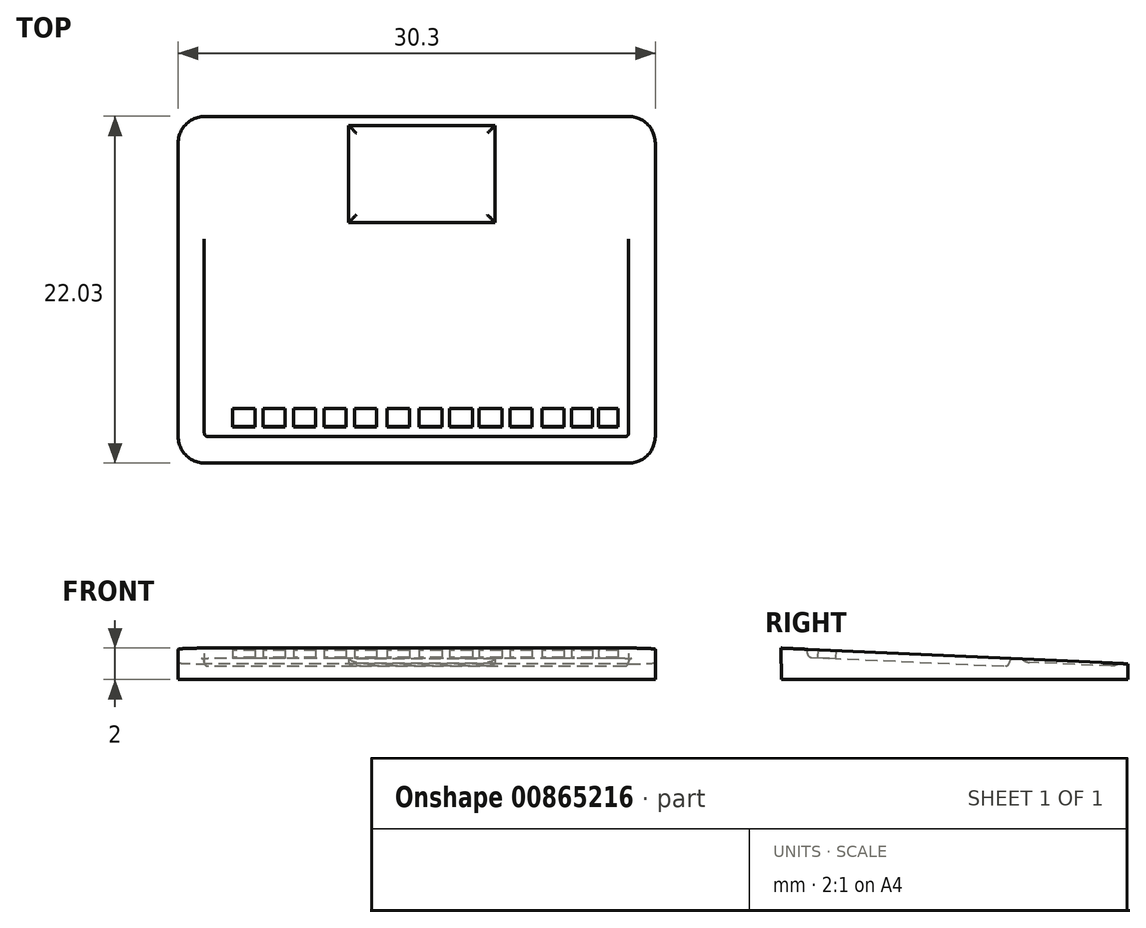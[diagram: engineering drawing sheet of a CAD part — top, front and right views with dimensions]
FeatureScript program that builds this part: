
annotation { "Feature Type Name" : "Feature", "Feature Type Description" : "" }
export const myFeature = defineFeature(function(context is Context, id is Id, definition is map)
    precondition{}
    {
        {
            var Q0;
            Q0=qCreatedBy(makeId("Right.planeOp"),FACE);
            var sketch = newSketch(context, id + "F0", { "sketchPlane" : qUnion([Q0])});
            skLineSegment(sketch, "E0", {"start": v(-240.72, 0) * mm, "end": v(-218.72, 0) * mm});
            skLineSegment(sketch, "E1", {"start": v(-218.72, 0) * mm, "end": v(-218.72, 1) * mm});
            skLineSegment(sketch, "E2", {"start": v(-218.72, 1) * mm, "end": v(-242.1, 41.92) * mm});
            skLineSegment(sketch, "E3", {"start": v(-242.1, 41.92) * mm, "end": v(-240.72, 0) * mm});
            skLineSegment(sketch, "E4", {"start": v(-44.13, 0) * mm, "end": v(-22.13, 0) * mm});
            skLineSegment(sketch, "E5", {"start": v(-22.13, 0) * mm, "end": v(-22.13, 1) * mm});
            skLineSegment(sketch, "E6", {"start": v(-22.13, 1) * mm, "end": v(-44.16, 2) * mm});
            skLineSegment(sketch, "E7", {"start": v(-44.16, 2) * mm, "end": v(-44.13, 0) * mm});
            skSolve(sketch);
        }
        {
            var Q0;
            Q0=makeQuery(id+"F0.imprint","IMPRINT",FACE,{"disambiguationData":[TD([[makeQuery(id+"F0.imprint","IMPRINT",EDGE,{"derivedFrom":sQuery(id+"F0.wireOp",EDGE,"E4")}),1.0]])]});
            extrude(context, id + "F1", {"entities" : qUnion([Q0]), "depth" : 30.3 * mm, "offsetDistance" : 25 * mm});
        }
        {
            var Q0;
            Q0=makeQuery(id+"F1.opExtrude","CAP_EDGE",EDGE,{"disambiguationData":[OSD([sQuery(id+"F0.wireOp",EDGE,"E5")])],"isStart":true});
            var Q1;
            Q1=makeQuery(id+"F1.opExtrude","CAP_EDGE",EDGE,{"disambiguationData":[OSD([sQuery(id+"F0.wireOp",EDGE,"E5")])],"isStart":false});
            var Q2;
            Q2=makeQuery(id+"F1.opExtrude","CAP_EDGE",EDGE,{"disambiguationData":[OSD([sQuery(id+"F0.wireOp",EDGE,"E7")])],"isStart":false});
            var Q3;
            Q3=makeQuery(id+"F1.opExtrude","CAP_EDGE",EDGE,{"disambiguationData":[OSD([sQuery(id+"F0.wireOp",EDGE,"E7")])],"isStart":true});
            fillet(context, id + "F2", {"entities" : qUnion([Q0, Q1, Q2, Q3]), "radius" : 1.69 * mm, "tangentPropagation" : true, "allowEdgeOverflow" : false});
        }
        {
            var Q0;
            Q0=makeQuery(id+"F1.opExtrude","SWEPT_FACE",FACE,{"disambiguationData":[OSD([sQuery(id+"F0.wireOp",EDGE,"E6")])]});
            var sketch = newSketch(context, id + "F3", { "sketchPlane" : qUnion([Q0])});
            skLineSegment(sketch, "E8.bottom", {"start": v(28.61, -42.52) * mm, "end": v(1.66, -42.52) * mm});
            skLineSegment(sketch, "E8.top", {"start": v(28.61, -29.7) * mm, "end": v(1.66, -29.7) * mm});
            skLineSegment(sketch, "E8.left", {"start": v(28.61, -42.52) * mm, "end": v(28.61, -29.7) * mm});
            skLineSegment(sketch, "E8.right", {"start": v(1.66, -42.52) * mm, "end": v(1.66, -29.7) * mm});
            skSolve(sketch);
        }
        {
            var Q0;
            Q0 = qSketchRegion(id + "F3", true);
            extrude(context, id + "F4", {"entities" : qUnion([Q0]), "operationType" : NewBodyOperationType.REMOVE, "oppositeDirection" : true, "depth" : 0.5 * mm, "offsetDistance" : 25 * mm});
        }
        {
            var Q0;
            Q0=makeQuery(id+"F4.boolean.opBoolean","COPY",FACE,{"derivedFrom":makeQuery(id+"F4.opExtrude","SWEPT_FACE",FACE,{"disambiguationData":[OSD([sQuery(id+"F3.wireOp",EDGE,"E8.bottom")])]})});
            var Q1;
            Q1=makeQuery(id+"F4.boolean.opBoolean","COPY",EDGE,{"derivedFrom":makeQuery(id+"F4.opExtrude","CAP_EDGE",EDGE,{"disambiguationData":[OSD([sQuery(id+"F3.wireOp",EDGE,"E8.right")])],"isStart":true})});
            var Q2;
            Q2=makeQuery(id+"F4.boolean.opBoolean","COPY",FACE,{"derivedFrom":makeQuery(id+"F4.opExtrude","SWEPT_FACE",FACE,{"disambiguationData":[OSD([sQuery(id+"F3.wireOp",EDGE,"E8.right")])]})});
            var Q3;
            Q3=makeQuery(id+"F4.boolean.opBoolean","COPY",FACE,{"derivedFrom":makeQuery(id+"F4.opExtrude","SWEPT_FACE",FACE,{"disambiguationData":[OSD([sQuery(id+"F3.wireOp",EDGE,"E8.top")])]})});
            var Q4;
            Q4=makeQuery(id+"F4.boolean.opBoolean","COPY",FACE,{"derivedFrom":makeQuery(id+"F4.opExtrude","SWEPT_FACE",FACE,{"disambiguationData":[OSD([sQuery(id+"F3.wireOp",EDGE,"E8.left")])]})});
            fillet(context, id + "F5", {"entities" : qUnion([Q0, Q1, Q2, Q3, Q4]), "radius" : 0.24 * mm, "tangentPropagation" : true, "allowEdgeOverflow" : false});
        }
        {
            var Q0;
            Q0=makeQuery(id+"F4.boolean.opBoolean","COPY",FACE,{"derivedFrom":makeQuery(id+"F4.opExtrude","CAP_FACE",FACE,{"disambiguationData":[OSD([sQuery(id+"F3.wireOp",EDGE,"E8.bottom"),sQuery(id+"F3.wireOp",EDGE,"E8.top"),sQuery(id+"F3.wireOp",EDGE,"E8.left"),sQuery(id+"F3.wireOp",EDGE,"E8.right")])],"isStart":false})});
            var sketch = newSketch(context, id + "F6", { "sketchPlane" : qUnion([Q0])});
            skLineSegment(sketch, "E9.bottom", {"start": v(27.93, -41.88) * mm, "end": v(26.7, -41.88) * mm});
            skLineSegment(sketch, "E9.top", {"start": v(27.93, -40.74) * mm, "end": v(26.7, -40.74) * mm});
            skLineSegment(sketch, "E9.left", {"start": v(27.93, -41.88) * mm, "end": v(27.93, -40.74) * mm});
            skLineSegment(sketch, "E9.right", {"start": v(26.7, -41.88) * mm, "end": v(26.7, -40.74) * mm});
            skPoint(sketch, "E10.firstSnap0", {"position": v(27.32, -41.88) * mm});
            skLineSegment(sketch, "E10.bottom", {"start": v(26.33, -41.88) * mm, "end": v(24.98, -41.88) * mm});
            skLineSegment(sketch, "E10.top", {"start": v(26.33, -40.73) * mm, "end": v(24.98, -40.73) * mm});
            skLineSegment(sketch, "E10.left", {"start": v(26.33, -41.88) * mm, "end": v(26.33, -40.73) * mm});
            skLineSegment(sketch, "E10.right", {"start": v(24.98, -41.88) * mm, "end": v(24.98, -40.73) * mm});
            skLineSegment(sketch, "E11.bottom", {"start": v(24.5, -41.88) * mm, "end": v(23.1, -41.88) * mm});
            skLineSegment(sketch, "E11.top", {"start": v(24.5, -40.73) * mm, "end": v(23.1, -40.73) * mm});
            skLineSegment(sketch, "E11.left", {"start": v(24.5, -41.88) * mm, "end": v(24.5, -40.73) * mm});
            skLineSegment(sketch, "E11.right", {"start": v(23.1, -41.88) * mm, "end": v(23.1, -40.73) * mm});
            skLineSegment(sketch, "E12.bottom", {"start": v(22.49, -41.88) * mm, "end": v(21.08, -41.88) * mm});
            skLineSegment(sketch, "E12.top", {"start": v(22.49, -40.73) * mm, "end": v(21.08, -40.73) * mm});
            skLineSegment(sketch, "E12.left", {"start": v(22.49, -41.88) * mm, "end": v(22.49, -40.73) * mm});
            skLineSegment(sketch, "E12.right", {"start": v(21.08, -41.88) * mm, "end": v(21.08, -40.73) * mm});
            skLineSegment(sketch, "E13.bottom", {"start": v(20.56, -41.88) * mm, "end": v(19.12, -41.88) * mm});
            skLineSegment(sketch, "E13.top", {"start": v(20.56, -40.73) * mm, "end": v(19.12, -40.73) * mm});
            skLineSegment(sketch, "E13.left", {"start": v(20.56, -41.88) * mm, "end": v(20.56, -40.73) * mm});
            skLineSegment(sketch, "E13.right", {"start": v(19.12, -41.88) * mm, "end": v(19.12, -40.73) * mm});
            skLineSegment(sketch, "E14.bottom", {"start": v(18.7, -41.88) * mm, "end": v(17.23, -41.88) * mm});
            skLineSegment(sketch, "E14.top", {"start": v(18.7, -40.73) * mm, "end": v(17.23, -40.73) * mm});
            skLineSegment(sketch, "E14.left", {"start": v(18.7, -41.88) * mm, "end": v(18.7, -40.73) * mm});
            skLineSegment(sketch, "E14.right", {"start": v(17.23, -41.88) * mm, "end": v(17.23, -40.73) * mm});
            skLineSegment(sketch, "E15.bottom", {"start": v(16.75, -41.88) * mm, "end": v(15.3, -41.88) * mm});
            skLineSegment(sketch, "E15.top", {"start": v(16.75, -40.73) * mm, "end": v(15.3, -40.73) * mm});
            skLineSegment(sketch, "E15.left", {"start": v(16.75, -41.88) * mm, "end": v(16.75, -40.73) * mm});
            skLineSegment(sketch, "E15.right", {"start": v(15.3, -41.88) * mm, "end": v(15.3, -40.73) * mm});
            skLineSegment(sketch, "E16.bottom", {"start": v(14.7, -41.88) * mm, "end": v(13.27, -41.88) * mm});
            skLineSegment(sketch, "E16.top", {"start": v(14.7, -40.73) * mm, "end": v(13.27, -40.73) * mm});
            skLineSegment(sketch, "E16.left", {"start": v(14.7, -41.88) * mm, "end": v(14.7, -40.73) * mm});
            skLineSegment(sketch, "E16.right", {"start": v(13.27, -41.88) * mm, "end": v(13.27, -40.73) * mm});
            skLineSegment(sketch, "E17.bottom", {"start": v(12.6, -41.88) * mm, "end": v(11.19, -41.88) * mm});
            skLineSegment(sketch, "E17.top", {"start": v(12.6, -40.73) * mm, "end": v(11.19, -40.73) * mm});
            skLineSegment(sketch, "E17.left", {"start": v(12.6, -41.88) * mm, "end": v(12.6, -40.73) * mm});
            skLineSegment(sketch, "E17.right", {"start": v(11.19, -41.88) * mm, "end": v(11.19, -40.73) * mm});
            skLineSegment(sketch, "E18.bottom", {"start": v(10.67, -41.88) * mm, "end": v(9.26, -41.88) * mm});
            skLineSegment(sketch, "E18.top", {"start": v(10.67, -40.73) * mm, "end": v(9.26, -40.73) * mm});
            skLineSegment(sketch, "E18.left", {"start": v(10.67, -41.88) * mm, "end": v(10.67, -40.73) * mm});
            skLineSegment(sketch, "E18.right", {"start": v(9.26, -41.88) * mm, "end": v(9.26, -40.73) * mm});
            skLineSegment(sketch, "E19.bottom", {"start": v(8.74, -41.88) * mm, "end": v(7.32, -41.88) * mm});
            skLineSegment(sketch, "E19.top", {"start": v(8.74, -40.73) * mm, "end": v(7.32, -40.73) * mm});
            skLineSegment(sketch, "E19.left", {"start": v(8.74, -41.88) * mm, "end": v(8.74, -40.73) * mm});
            skLineSegment(sketch, "E19.right", {"start": v(7.32, -41.88) * mm, "end": v(7.32, -40.73) * mm});
            skLineSegment(sketch, "E20.bottom", {"start": v(6.79, -41.88) * mm, "end": v(5.38, -41.88) * mm});
            skLineSegment(sketch, "E20.top", {"start": v(6.79, -40.73) * mm, "end": v(5.38, -40.73) * mm});
            skLineSegment(sketch, "E20.left", {"start": v(6.79, -41.88) * mm, "end": v(6.79, -40.73) * mm});
            skLineSegment(sketch, "E20.right", {"start": v(5.38, -41.88) * mm, "end": v(5.38, -40.73) * mm});
            skLineSegment(sketch, "E21.bottom", {"start": v(4.9, -41.88) * mm, "end": v(3.46, -41.88) * mm});
            skLineSegment(sketch, "E21.top", {"start": v(4.9, -40.73) * mm, "end": v(3.46, -40.73) * mm});
            skLineSegment(sketch, "E21.left", {"start": v(4.9, -41.88) * mm, "end": v(4.9, -40.73) * mm});
            skLineSegment(sketch, "E21.right", {"start": v(3.46, -41.88) * mm, "end": v(3.46, -40.73) * mm});
            skSolve(sketch);
        }
        {
            var Q0;
            Q0 = qSketchRegion(id + "F6", true);
            extrude(context, id + "F7", {"entities" : qUnion([Q0]), "operationType" : NewBodyOperationType.ADD, "depth" : 0.5 * mm, "offsetDistance" : 25 * mm});
        }
        {
            var Q0;
            Q0=makeQuery(id+"F1.opExtrude","SWEPT_FACE",FACE,{"disambiguationData":[OSD([sQuery(id+"F0.wireOp",EDGE,"E6")])]});
            var sketch = newSketch(context, id + "F8", { "sketchPlane" : qUnion([Q0])});
            skLineSegment(sketch, "E22.bottom", {"start": v(20.13, -28.9) * mm, "end": v(10.83, -28.9) * mm});
            skLineSegment(sketch, "E22.top", {"start": v(20.13, -22.74) * mm, "end": v(10.83, -22.74) * mm});
            skLineSegment(sketch, "E22.left", {"start": v(20.13, -28.9) * mm, "end": v(20.13, -22.74) * mm});
            skLineSegment(sketch, "E22.right", {"start": v(10.83, -28.9) * mm, "end": v(10.83, -22.74) * mm});
            skSolve(sketch);
        }
        {
            var Q0;
            Q0 = qSketchRegion(id + "F8", true);
            extrude(context, id + "F9", {"entities" : qUnion([Q0]), "operationType" : NewBodyOperationType.REMOVE, "oppositeDirection" : true, "depth" : 0.19 * mm, "offsetDistance" : 25 * mm});
        }
        {
            var Q0;
            Q0=makeQuery(id+"F9.boolean.opBoolean","COPY",EDGE,{"derivedFrom":makeQuery(id+"F9.opExtrude","CAP_EDGE",EDGE,{"disambiguationData":[OSD([sQuery(id+"F8.wireOp",EDGE,"E22.bottom")])],"isStart":false})});
            var Q1;
            Q1=makeQuery(id+"F9.boolean.opBoolean","COPY",EDGE,{"derivedFrom":makeQuery(id+"F9.opExtrude","CAP_EDGE",EDGE,{"disambiguationData":[OSD([sQuery(id+"F8.wireOp",EDGE,"E22.right")])],"isStart":false})});
            var Q2;
            Q2=makeQuery(id+"F9.boolean.opBoolean","COPY",EDGE,{"derivedFrom":makeQuery(id+"F9.opExtrude","CAP_EDGE",EDGE,{"disambiguationData":[OSD([sQuery(id+"F8.wireOp",EDGE,"E22.left")])],"isStart":false})});
            var Q3;
            Q3=makeQuery(id+"F9.boolean.opBoolean","COPY",EDGE,{"derivedFrom":makeQuery(id+"F9.opExtrude","CAP_EDGE",EDGE,{"disambiguationData":[OSD([sQuery(id+"F8.wireOp",EDGE,"E22.top")])],"isStart":false})});
            fillet(context, id + "F10", {"entities" : qUnion([Q0, Q1, Q2, Q3]), "radius" : 0.72 * mm, "tangentPropagation" : true, "allowEdgeOverflow" : false});
        }
    });
